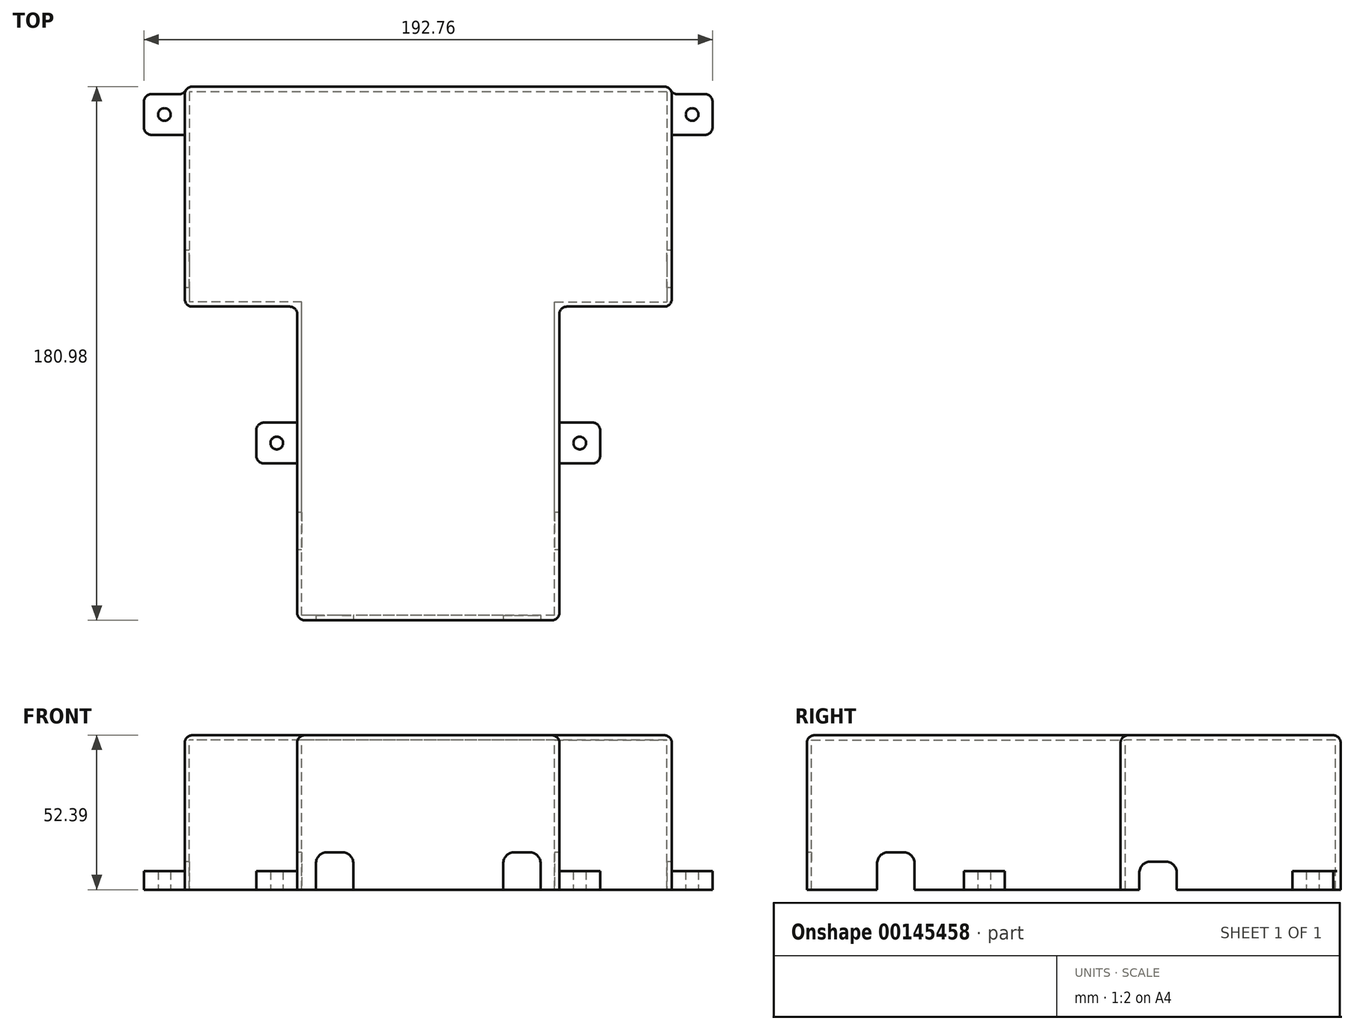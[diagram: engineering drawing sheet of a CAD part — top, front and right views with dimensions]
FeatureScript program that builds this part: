
annotation { "Feature Type Name" : "Feature", "Feature Type Description" : "" }
export const myFeature = defineFeature(function(context is Context, id is Id, definition is map)
    precondition{}
    {
        {
            var Q0;
            Q0=qCreatedBy(makeId("Top.planeOp"),FACE);
            var sketch = newSketch(context, id + "F0", { "sketchPlane" : qUnion([Q0])});
            skLineSegment(sketch, "E0.bottom", {"start": v(-82.55, 90.49) * mm, "end": v(82.55, 90.49) * mm});
            skLineSegment(sketch, "E0.top", {"start": v(-82.55, -90.49) * mm, "end": v(82.55, -90.49) * mm});
            skLineSegment(sketch, "E0.left", {"start": v(-82.55, 90.49) * mm, "end": v(-82.55, -90.49) * mm});
            skLineSegment(sketch, "E0.right", {"start": v(82.55, 90.49) * mm, "end": v(82.55, -90.49) * mm});
            skPoint(sketch, "E0.middle", {"position": v(0, 0) * mm});
            skLineSegment(sketch, "E1.bottom", {"start": v(-76.2, 85.72) * mm, "end": v(76.2, 85.72) * mm, "construction": true});
            skLineSegment(sketch, "E1.top", {"start": v(-76.2, 34.92) * mm, "end": v(76.2, 34.92) * mm, "construction": true});
            skLineSegment(sketch, "E1.left", {"start": v(-76.2, 85.72) * mm, "end": v(-76.2, 34.92) * mm, "construction": true});
            skLineSegment(sketch, "E1.right", {"start": v(76.2, 85.73) * mm, "end": v(76.2, 34.93) * mm, "construction": true});
            skPoint(sketch, "E1.middle", {"position": v(0, 60.32) * mm});
            skLineSegment(sketch, "E2.bottom", {"start": v(-47.62, -3.18) * mm, "end": v(-9.52, -3.18) * mm, "construction": true});
            skLineSegment(sketch, "E2.top", {"start": v(-47.62, -85.73) * mm, "end": v(-9.52, -85.73) * mm, "construction": true});
            skLineSegment(sketch, "E2.left", {"start": v(-47.62, -3.18) * mm, "end": v(-47.62, -85.73) * mm, "construction": true});
            skLineSegment(sketch, "E2.right", {"start": v(-9.52, -3.18) * mm, "end": v(-9.52, -85.73) * mm, "construction": true});
            skPoint(sketch, "E2.middle", {"position": v(-28.57, -44.45) * mm});
            skPoint(sketch, "E3.MirrorP", {"position": v(28.57, -44.45) * mm});
            skLineSegment(sketch, "E4.MirrorCS", {"start": v(47.62, -3.18) * mm, "end": v(47.62, -85.73) * mm, "construction": true});
            skLineSegment(sketch, "E5.MirrorCS", {"start": v(47.62, -85.73) * mm, "end": v(9.52, -85.73) * mm, "construction": true});
            skLineSegment(sketch, "E6.MirrorCS", {"start": v(47.62, -3.18) * mm, "end": v(9.52, -3.18) * mm, "construction": true});
            skLineSegment(sketch, "E7", {"start": v(0, 85.72) * mm, "end": v(0, 90.49) * mm, "construction": true});
            skLineSegment(sketch, "E8", {"start": v(-28.57, -85.73) * mm, "end": v(-28.57, -90.49) * mm, "construction": true});
            skLineSegment(sketch, "E9", {"start": v(-82.55, 15.87) * mm, "end": v(-44.45, 15.87) * mm});
            skLineSegment(sketch, "E10", {"start": v(-44.45, 15.87) * mm, "end": v(-44.45, -90.49) * mm});
            skLineSegment(sketch, "E11.MirrorCS", {"start": v(44.45, 15.87) * mm, "end": v(44.45, -90.49) * mm});
            skLineSegment(sketch, "E12.MirrorCS", {"start": v(82.55, 15.87) * mm, "end": v(44.45, 15.87) * mm});
            skLineSegment(sketch, "E13.bottom", {"start": v(-8.25, -90.49) * mm, "end": v(-6.67, -90.49) * mm});
            skLineSegment(sketch, "E13.top", {"start": v(-8.25, 0) * mm, "end": v(-6.67, 0) * mm});
            skLineSegment(sketch, "E13.right", {"start": v(-6.67, -90.49) * mm, "end": v(-6.67, 0) * mm});
            skLineSegment(sketch, "E14.MirrorCS", {"start": v(8.25, -90.49) * mm, "end": v(8.25, 0) * mm});
            skLineSegment(sketch, "E15.MirrorCS", {"start": v(8.25, 0) * mm, "end": v(6.67, 0) * mm});
            skLineSegment(sketch, "E16.MirrorCS", {"start": v(8.25, -90.49) * mm, "end": v(6.67, -90.49) * mm});
            skLineSegment(sketch, "E17.MirrorCS", {"start": v(9.52, -3.18) * mm, "end": v(9.52, -85.73) * mm, "construction": true});
            skLineSegment(sketch, "E18.bottom", {"start": v(-66.67, 34.13) * mm, "end": v(-41.27, 34.13) * mm});
            skLineSegment(sketch, "E18.top", {"start": v(-66.67, 30.96) * mm, "end": v(-41.27, 30.96) * mm});
            skLineSegment(sketch, "E18.left", {"start": v(-66.68, 34.13) * mm, "end": v(-66.68, 30.96) * mm});
            skLineSegment(sketch, "E18.right", {"start": v(-41.28, 34.13) * mm, "end": v(-41.28, 30.96) * mm});
            skPoint(sketch, "E18.middle", {"position": v(-53.97, 32.54) * mm});
            skLineSegment(sketch, "E19", {"start": v(0, 60.32) * mm, "end": v(-14.3, 60.32) * mm, "construction": true});
            skPoint(sketch, "E20.MirrorP", {"position": v(-53.98, 88.1) * mm});
            skLineSegment(sketch, "E21.MirrorCS", {"start": v(-66.68, 89.7) * mm, "end": v(-41.27, 89.7) * mm});
            skLineSegment(sketch, "E22.MirrorCS", {"start": v(-41.28, 86.52) * mm, "end": v(-41.28, 89.7) * mm});
            skLineSegment(sketch, "E23.MirrorCS", {"start": v(-66.68, 86.52) * mm, "end": v(-66.68, 89.7) * mm});
            skLineSegment(sketch, "E24.MirrorCS", {"start": v(-66.67, 86.52) * mm, "end": v(-41.27, 86.52) * mm});
            skPoint(sketch, "E25.MirrorP", {"position": v(53.98, 32.54) * mm});
            skLineSegment(sketch, "E26.MirrorCS", {"start": v(66.67, 86.52) * mm, "end": v(41.27, 86.52) * mm});
            skLineSegment(sketch, "E27.MirrorCS", {"start": v(66.68, 89.7) * mm, "end": v(41.27, 89.7) * mm});
            skPoint(sketch, "E28.MirrorP", {"position": v(53.98, 88.1) * mm});
            skLineSegment(sketch, "E29.MirrorCS", {"start": v(41.28, 86.52) * mm, "end": v(41.28, 89.7) * mm});
            skLineSegment(sketch, "E30.MirrorCS", {"start": v(66.68, 86.52) * mm, "end": v(66.68, 89.7) * mm});
            skLineSegment(sketch, "E31.MirrorCS", {"start": v(41.28, 34.13) * mm, "end": v(41.28, 30.96) * mm});
            skLineSegment(sketch, "E32.MirrorCS", {"start": v(66.68, 34.13) * mm, "end": v(66.68, 30.96) * mm});
            skLineSegment(sketch, "E33.MirrorCS", {"start": v(66.68, 34.13) * mm, "end": v(41.28, 34.13) * mm});
            skLineSegment(sketch, "E34.MirrorCS", {"start": v(66.68, 30.96) * mm, "end": v(41.28, 30.96) * mm});
            skSolve(sketch);
        }
        {
            var Q0;
            Q0=makeQuery(id+"F0.imprint","IMPRINT",FACE,{"disambiguationData":[TD([[makeQuery(id+"F0.imprint","IMPRINT",EDGE,{"derivedFrom":sQuery(id+"F0.wireOp",EDGE,"E13.bottom")}),1.0]])]});
            var Q1;
            Q1=makeQuery(id+"F0.imprint","IMPRINT",FACE,{"disambiguationData":[TD([[makeQuery(id+"F0.imprint","IMPRINT",EDGE,{"derivedFrom":sQuery(id+"F0.wireOp",EDGE,"E14.MirrorCS")}),1.0]])]});
            var Q2;
            Q2=makeQuery(id+"F0.imprint","IMPRINT",FACE,{"disambiguationData":[TD([[makeQuery(id+"F0.imprint","IMPRINT",EDGE,{"derivedFrom":sQuery(id+"F0.wireOp",EDGE,"E21.MirrorCS")}),-1.0]])]});
            var Q3;
            Q3=makeQuery(id+"F0.imprint","IMPRINT",FACE,{"disambiguationData":[TD([[makeQuery(id+"F0.imprint","IMPRINT",EDGE,{"derivedFrom":sQuery(id+"F0.wireOp",EDGE,"E18.bottom")}),-1.0]])]});
            var Q4;
            Q4=makeQuery(id+"F0.imprint","IMPRINT",FACE,{"disambiguationData":[TD([[makeQuery(id+"F0.imprint","IMPRINT",EDGE,{"derivedFrom":sQuery(id+"F0.wireOp",EDGE,"E26.MirrorCS")}),-1.0]])]});
            var Q5;
            {var subQ10=sQuery(id+"F0.wireOp",EDGE,"E0.bottom");Q5=makeQuery(id+"F0.imprint","IMPRINT",FACE,{"disambiguationData":[TD([[makeQuery(id+"F0.imprint","IMPRINT",EDGE,{"derivedFrom":subQ10}),-1.0]])]});}
            var Q6;
            Q6=makeQuery(id+"F0.imprint","IMPRINT",FACE,{"disambiguationData":[TD([[makeQuery(id+"F0.imprint","IMPRINT",EDGE,{"derivedFrom":sQuery(id+"F0.wireOp",EDGE,"E31.MirrorCS")}),1.0]])]});
            extrude(context, id + "F1", {"entities" : qUnion([Q0, Q1, Q2, Q3, Q4, Q5, Q6]), "depth" : 1.59 * mm});
        }
        {
            var Q0;
            Q0=makeQuery(id+"F1.opExtrude","CAP_FACE",FACE,{"disambiguationData":[OSD([sQuery(id+"F0.wireOp",EDGE,"E0.bottom"),sQuery(id+"F0.wireOp",EDGE,"E0.top"),sQuery(id+"F0.wireOp",EDGE,"E0.left"),sQuery(id+"F0.wireOp",EDGE,"E0.right"),sQuery(id+"F0.wireOp",EDGE,"E9"),sQuery(id+"F0.wireOp",EDGE,"E10"),sQuery(id+"F0.wireOp",EDGE,"E11.MirrorCS"),sQuery(id+"F0.wireOp",EDGE,"E12.MirrorCS")])],"isStart":true});
            var sketch = newSketch(context, id + "F2", { "sketchPlane" : qUnion([Q0])});
            skLineSegment(sketch, "E35", {"start": v(0, 88.9) * mm, "end": v(-42.86, 88.9) * mm});
            skLineSegment(sketch, "E36", {"start": v(-42.86, 88.9) * mm, "end": v(-42.86, -17.46) * mm});
            skLineSegment(sketch, "E37", {"start": v(-42.86, -17.46) * mm, "end": v(-80.96, -17.46) * mm});
            skLineSegment(sketch, "E38", {"start": v(-80.96, -88.7) * mm, "end": v(0, -88.7) * mm});
            skLineSegment(sketch, "E39", {"start": v(-40.48, -88.7) * mm, "end": v(-40.48, -90.3) * mm, "construction": true});
            skLineSegment(sketch, "E40", {"start": v(-80.96, -53.08) * mm, "end": v(-82.55, -53.08) * mm, "construction": true});
            skLineSegment(sketch, "E41", {"start": v(-61.91, -17.46) * mm, "end": v(-61.91, -15.87) * mm, "construction": true});
            skLineSegment(sketch, "E42", {"start": v(-42.86, 35.72) * mm, "end": v(-44.45, 35.72) * mm});
            skLineSegment(sketch, "E43", {"start": v(-21.43, 88.9) * mm, "end": v(-21.43, 90.49) * mm, "construction": true});
            skLineSegment(sketch, "E44.MirrorCS", {"start": v(40.48, -88.7) * mm, "end": v(40.48, -90.3) * mm, "construction": true});
            skLineSegment(sketch, "E45.MirrorCS", {"start": v(80.96, -53.08) * mm, "end": v(82.55, -53.08) * mm, "construction": true});
            skLineSegment(sketch, "E46.MirrorCS", {"start": v(61.91, -17.46) * mm, "end": v(61.91, -15.87) * mm, "construction": true});
            skLineSegment(sketch, "E47.MirrorCS", {"start": v(42.86, 35.72) * mm, "end": v(44.45, 35.72) * mm});
            skLineSegment(sketch, "E48.MirrorCS", {"start": v(21.43, 88.9) * mm, "end": v(21.43, 90.49) * mm, "construction": true});
            skLineSegment(sketch, "E49.MirrorCS", {"start": v(80.96, -88.7) * mm, "end": v(0, -88.7) * mm});
            skLineSegment(sketch, "E50.MirrorCS", {"start": v(42.86, -17.46) * mm, "end": v(80.96, -17.46) * mm});
            skLineSegment(sketch, "E51.MirrorCS", {"start": v(0, 88.9) * mm, "end": v(42.86, 88.9) * mm});
            skLineSegment(sketch, "E52.MirrorCS", {"start": v(42.86, 88.9) * mm, "end": v(42.86, -17.46) * mm});
            skLineSegment(sketch, "E53", {"start": v(-80.96, -88.7) * mm, "end": v(-80.96, -17.46) * mm});
            skLineSegment(sketch, "E54.MirrorCS", {"start": v(80.96, -88.7) * mm, "end": v(80.96, -17.46) * mm});
            skSolve(sketch);
        }
        {
            var Q0;
            {var subQ3=sQuery(id+"F2.wireOp",EDGE,"E35");Q0=makeQuery(id+"F2.imprint","IMPRINT",FACE,{"disambiguationData":[TD([[makeQuery(id+"F2.imprint","IMPRINT",EDGE,{"derivedFrom":subQ3}),-1.0]])]});}
            var Q1;
            {var subQ4=sQuery(id+"F2.wireOp",EDGE,"E37");Q1=makeQuery(id+"F2.imprint","IMPRINT",FACE,{"disambiguationData":[TD([[makeQuery(id+"F2.imprint","IMPRINT",EDGE,{"derivedFrom":subQ4}),-1.0]])]});}
            var Q2;
            {var subQ9=sQuery(id+"F2.wireOp",EDGE,"E42");Q2=makeQuery(id+"F2.imprint","IMPRINT",FACE,{"disambiguationData":[TD([[makeQuery(id+"F2.imprint","IMPRINT",EDGE,{"derivedFrom":subQ9}),-1.0]])]});}
            var Q3;
            {var subQ11=sQuery(id+"F2.wireOp",EDGE,"E47.MirrorCS");Q3=makeQuery(id+"F2.imprint","IMPRINT",FACE,{"disambiguationData":[TD([[makeQuery(id+"F2.imprint","IMPRINT",EDGE,{"derivedFrom":subQ11}),1.0]])]});}
            extrude(context, id + "F3", {"entities" : qUnion([Q0, Q1, Q2, Q3]), "operationType" : NewBodyOperationType.ADD, "offsetDistance" : 25.4 * mm, "depth" : 50.8 * mm});
        }
        {
            var Q0;
            {var subQ0=sQuery(id+"F0.wireOp",EDGE,"E0.top");Q0=makeQuery(id+"F3.boolean.opBoolean","MERGE",FACE,{"derivedFrom":[makeQuery(id+"F1.opExtrude","SWEPT_FACE",FACE,{"disambiguationData":[OSD([subQ0])]}),makeQuery(id+"F3.opExtrude","SWEPT_FACE",FACE,{"disambiguationData":[OSD([subQ0])]})]});}
            var sketch = newSketch(context, id + "F4", { "sketchPlane" : qUnion([Q0])});
            skLineSegment(sketch, "E55", {"start": v(0, -24.6) * mm, "end": v(-25.4, -24.6) * mm, "construction": true});
            skPoint(sketch, "E55.startSnap0", {"position": v(-44.45, -24.6) * mm});
            skLineSegment(sketch, "E56.bottom", {"start": v(-25.4, -50.8) * mm, "end": v(-38.1, -50.8) * mm});
            skLineSegment(sketch, "E56.top", {"start": v(-29.21, -38.1) * mm, "end": v(-34.29, -38.1) * mm});
            skLineSegment(sketch, "E56.left", {"start": v(-25.4, -50.8) * mm, "end": v(-25.4, -41.91) * mm});
            skLineSegment(sketch, "E56.right", {"start": v(-38.1, -50.8) * mm, "end": v(-38.1, -41.91) * mm});
            skLineSegment(sketch, "E57.MirrorCS", {"start": v(25.4, -50.8) * mm, "end": v(25.4, -41.9) * mm});
            skLineSegment(sketch, "E58.MirrorCS", {"start": v(25.4, -50.8) * mm, "end": v(38.1, -50.8) * mm});
            skLineSegment(sketch, "E59.MirrorCS", {"start": v(29.21, -38.1) * mm, "end": v(34.29, -38.1) * mm});
            skLineSegment(sketch, "E60.MirrorCS", {"start": v(38.1, -50.8) * mm, "end": v(38.1, -41.91) * mm});
            skPoint(sketch, "E61.visualSharp", {"position": v(-38.1, -38.1) * mm});
            skArc(sketch, "E61.filletArc", {"start": v(-34.29, -38.1) * mm, "mid": v(-36.98, -39.22) * mm, "end": v(-38.1, -41.91) * mm});
            skPoint(sketch, "E62.visualSharp", {"position": v(-25.4, -38.1) * mm});
            skArc(sketch, "E62.filletArc", {"start": v(-25.4, -41.91) * mm, "mid": v(-26.52, -39.22) * mm, "end": v(-29.21, -38.1) * mm});
            skPoint(sketch, "E63.visualSharp", {"position": v(25.4, -38.1) * mm});
            skArc(sketch, "E63.filletArc", {"start": v(29.21, -38.1) * mm, "mid": v(26.52, -39.22) * mm, "end": v(25.4, -41.9) * mm});
            skPoint(sketch, "E64.visualSharp", {"position": v(38.1, -38.1) * mm});
            skArc(sketch, "E64.filletArc", {"start": v(38.1, -41.91) * mm, "mid": v(36.98, -39.22) * mm, "end": v(34.29, -38.1) * mm});
            skSolve(sketch);
        }
        {
            var Q0;
            Q0 = qSketchRegion(id + "F4", true);
            var Q1;
            Q1=makeQuery(id+"F3.opExtrude","SWEPT_FACE",FACE,{"disambiguationData":[OSD([sQuery(id+"F2.wireOp",EDGE,"E35"),sQuery(id+"F2.wireOp",EDGE,"E51.MirrorCS")])]});
            extrude(context, id + "F5", {"entities" : qUnion([Q0]), "operationType" : NewBodyOperationType.REMOVE, "endBound" : BoundingType.UP_TO_SURFACE, "oppositeDirection" : true, "endBoundEntityFace" : qUnion([Q1]), "depth" : 25.4 * mm});
        }
        {
            var Q0;
            {var subQ0=sQuery(id+"F0.wireOp",EDGE,"E0.left");Q0=makeQuery(id+"F3.boolean.opBoolean","MERGE",FACE,{"derivedFrom":[makeQuery(id+"F1.opExtrude","SWEPT_FACE",FACE,{"disambiguationData":[OSD([subQ0])]}),makeQuery(id+"F3.opExtrude","SWEPT_FACE",FACE,{"disambiguationData":[OSD([subQ0])]})]});}
            var sketch = newSketch(context, id + "F6", { "sketchPlane" : qUnion([Q0])});
            skPoint(sketch, "E65.0", {"position": v(-34.92, 0) * mm});
            skLineSegment(sketch, "E66.bottom", {"start": v(-31.11, -41.28) * mm, "end": v(-26.03, -41.28) * mm});
            skLineSegment(sketch, "E66.top", {"start": v(-34.92, -50.8) * mm, "end": v(-22.22, -50.8) * mm});
            skLineSegment(sketch, "E66.left", {"start": v(-34.92, -45.09) * mm, "end": v(-34.92, -50.8) * mm});
            skLineSegment(sketch, "E66.right", {"start": v(-22.22, -45.09) * mm, "end": v(-22.22, -50.8) * mm});
            skPoint(sketch, "E67.visualSharp", {"position": v(-34.92, -41.28) * mm});
            skArc(sketch, "E67.filletArc", {"start": v(-31.11, -41.28) * mm, "mid": v(-33.8, -42.4) * mm, "end": v(-34.92, -45.09) * mm});
            skPoint(sketch, "E68.visualSharp", {"position": v(-22.22, -41.28) * mm});
            skArc(sketch, "E68.filletArc", {"start": v(-22.22, -45.09) * mm, "mid": v(-23.34, -42.4) * mm, "end": v(-26.03, -41.28) * mm});
            skSolve(sketch);
        }
        {
            var Q0;
            Q0=makeQuery(id+"F6.imprint","IMPRINT",FACE,{"disambiguationData":[TD([[makeQuery(id+"F6.imprint","IMPRINT",EDGE,{"derivedFrom":sQuery(id+"F6.wireOp",EDGE,"E66.bottom")}),-1.0]])]});
            var Q1;
            {var subQ0=sQuery(id+"F0.wireOp",EDGE,"E0.right");Q1=makeQuery(id+"F3.boolean.opBoolean","MERGE",FACE,{"derivedFrom":[makeQuery(id+"F1.opExtrude","SWEPT_FACE",FACE,{"disambiguationData":[OSD([subQ0])]}),makeQuery(id+"F3.opExtrude","SWEPT_FACE",FACE,{"disambiguationData":[OSD([subQ0])]})]});}
            extrude(context, id + "F7", {"entities" : qUnion([Q0]), "operationType" : NewBodyOperationType.REMOVE, "endBound" : BoundingType.UP_TO_SURFACE, "oppositeDirection" : true, "endBoundEntityFace" : qUnion([Q1]), "depth" : 25.4 * mm});
        }
        {
            var Q0;
            {var subQ0=sQuery(id+"F0.wireOp",EDGE,"E10");Q0=makeQuery(id+"F3.boolean.opBoolean","MERGE",FACE,{"derivedFrom":[makeQuery(id+"F1.opExtrude","SWEPT_FACE",FACE,{"disambiguationData":[OSD([subQ0])]}),makeQuery(id+"F3.opExtrude","SWEPT_FACE",FACE,{"disambiguationData":[OSD([subQ0])]})]});}
            var sketch = newSketch(context, id + "F8", { "sketchPlane" : qUnion([Q0])});
            skPoint(sketch, "E69.0", {"position": v(85.73, 0) * mm});
            skLineSegment(sketch, "E70", {"start": v(85.73, 0) * mm, "end": v(66.68, 0) * mm, "construction": true});
            skLineSegment(sketch, "E71.bottom", {"start": v(66.68, -50.8) * mm, "end": v(53.98, -50.8) * mm});
            skLineSegment(sketch, "E71.top", {"start": v(62.87, -38.1) * mm, "end": v(57.79, -38.1) * mm});
            skLineSegment(sketch, "E71.left", {"start": v(66.68, -50.8) * mm, "end": v(66.68, -41.91) * mm});
            skLineSegment(sketch, "E71.right", {"start": v(53.98, -50.8) * mm, "end": v(53.98, -41.91) * mm});
            skPoint(sketch, "E72.visualSharp", {"position": v(53.98, -38.1) * mm});
            skArc(sketch, "E72.filletArc", {"start": v(57.79, -38.1) * mm, "mid": v(55.1, -39.22) * mm, "end": v(53.98, -41.91) * mm});
            skPoint(sketch, "E73.visualSharp", {"position": v(66.68, -38.1) * mm});
            skArc(sketch, "E73.filletArc", {"start": v(66.68, -41.91) * mm, "mid": v(65.56, -39.22) * mm, "end": v(62.87, -38.1) * mm});
            skSolve(sketch);
        }
        {
            var Q0;
            Q0 = qSketchRegion(id + "F8", true);
            var Q1;
            {var subQ0=sQuery(id+"F0.wireOp",EDGE,"E11.MirrorCS");Q1=makeQuery(id+"F3.boolean.opBoolean","MERGE",FACE,{"derivedFrom":[makeQuery(id+"F1.opExtrude","SWEPT_FACE",FACE,{"disambiguationData":[OSD([subQ0])]}),makeQuery(id+"F3.opExtrude","SWEPT_FACE",FACE,{"disambiguationData":[OSD([subQ0])]})]});}
            extrude(context, id + "F9", {"entities" : qUnion([Q0]), "operationType" : NewBodyOperationType.REMOVE, "endBound" : BoundingType.UP_TO_SURFACE, "oppositeDirection" : true, "endBoundEntityFace" : qUnion([Q1]), "depth" : 25.4 * mm});
        }
        {
            var Q0;
            Q0=makeQuery(id+"F1.opExtrude","CAP_EDGE",EDGE,{"disambiguationData":[OSD([sQuery(id+"F0.wireOp",EDGE,"E0.left")])],"isStart":false});
            var Q1;
            Q1=makeQuery(id+"F1.opExtrude","CAP_EDGE",EDGE,{"disambiguationData":[OSD([sQuery(id+"F0.wireOp",EDGE,"E10")])],"isStart":false});
            var Q2;
            Q2=makeQuery(id+"F1.opExtrude","CAP_EDGE",EDGE,{"disambiguationData":[OSD([sQuery(id+"F0.wireOp",EDGE,"E9")])],"isStart":false});
            var Q3;
            Q3=makeQuery(id+"F1.opExtrude","CAP_EDGE",EDGE,{"disambiguationData":[OSD([sQuery(id+"F0.wireOp",EDGE,"E0.top"),sQuery(id+"F0.wireOp",EDGE,"E13.bottom"),sQuery(id+"F0.wireOp",EDGE,"E16.MirrorCS")])],"isStart":false});
            var Q4;
            Q4=makeQuery(id+"F1.opExtrude","CAP_EDGE",EDGE,{"disambiguationData":[OSD([sQuery(id+"F0.wireOp",EDGE,"E11.MirrorCS")])],"isStart":false});
            var Q5;
            Q5=makeQuery(id+"F1.opExtrude","CAP_EDGE",EDGE,{"disambiguationData":[OSD([sQuery(id+"F0.wireOp",EDGE,"E12.MirrorCS")])],"isStart":false});
            var Q6;
            Q6=makeQuery(id+"F1.opExtrude","CAP_EDGE",EDGE,{"disambiguationData":[OSD([sQuery(id+"F0.wireOp",EDGE,"E0.right")])],"isStart":false});
            var Q7;
            Q7=makeQuery(id+"F1.opExtrude","CAP_EDGE",EDGE,{"disambiguationData":[OSD([sQuery(id+"F0.wireOp",EDGE,"E0.bottom")])],"isStart":false});
            var Q8;
            {var subQ0=sQuery(id+"F0.wireOp",EDGE,"E0.right");var subQ1=sQuery(id+"F0.wireOp",EDGE,"E0.bottom");Q8=makeQuery(id+"F3.boolean.opBoolean","MERGE",EDGE,{"derivedFrom":[makeQuery(id+"F1.opExtrude","SWEPT_EDGE",EDGE,{"disambiguationData":[OSD([subQ1,subQ0])]}),makeQuery(id+"F3.opExtrude","SWEPT_EDGE",EDGE,{"disambiguationData":[OSD([subQ1,subQ0])]})]});}
            var Q9;
            {var subQ0=sQuery(id+"F0.wireOp",EDGE,"E0.left");var subQ1=sQuery(id+"F0.wireOp",EDGE,"E0.bottom");Q9=makeQuery(id+"F3.boolean.opBoolean","MERGE",EDGE,{"derivedFrom":[makeQuery(id+"F1.opExtrude","SWEPT_EDGE",EDGE,{"disambiguationData":[OSD([subQ1,subQ0])]}),makeQuery(id+"F3.opExtrude","SWEPT_EDGE",EDGE,{"disambiguationData":[OSD([subQ1,subQ0])]})]});}
            var Q10;
            {var subQ0=sQuery(id+"F0.wireOp",EDGE,"E9");var subQ1=sQuery(id+"F0.wireOp",EDGE,"E0.left");Q10=makeQuery(id+"F3.boolean.opBoolean","MERGE",EDGE,{"derivedFrom":[makeQuery(id+"F1.opExtrude","SWEPT_EDGE",EDGE,{"disambiguationData":[OSD([subQ1,subQ0])]}),makeQuery(id+"F3.opExtrude","SWEPT_EDGE",EDGE,{"disambiguationData":[OSD([subQ1,subQ0])]})]});}
            var Q11;
            {var subQ0=sQuery(id+"F0.wireOp",EDGE,"E10");var subQ1=sQuery(id+"F0.wireOp",EDGE,"E9");Q11=makeQuery(id+"F3.boolean.opBoolean","MERGE",EDGE,{"derivedFrom":[makeQuery(id+"F1.opExtrude","SWEPT_EDGE",EDGE,{"disambiguationData":[OSD([subQ1,subQ0])]}),makeQuery(id+"F3.opExtrude","SWEPT_EDGE",EDGE,{"disambiguationData":[OSD([subQ1,subQ0])]})]});}
            var Q12;
            {var subQ0=sQuery(id+"F0.wireOp",EDGE,"E10");var subQ1=sQuery(id+"F0.wireOp",EDGE,"E0.top");Q12=makeQuery(id+"F3.boolean.opBoolean","MERGE",EDGE,{"derivedFrom":[makeQuery(id+"F1.opExtrude","SWEPT_EDGE",EDGE,{"disambiguationData":[OSD([subQ1,subQ0])]}),makeQuery(id+"F3.opExtrude","SWEPT_EDGE",EDGE,{"disambiguationData":[OSD([subQ1,subQ0,sQuery(id+"F0.wireOp",EDGE,"E13.bottom"),sQuery(id+"F0.wireOp",EDGE,"E16.MirrorCS")])]})]});}
            var Q13;
            {var subQ0=sQuery(id+"F0.wireOp",EDGE,"E11.MirrorCS");var subQ1=sQuery(id+"F0.wireOp",EDGE,"E0.top");Q13=makeQuery(id+"F3.boolean.opBoolean","MERGE",EDGE,{"derivedFrom":[makeQuery(id+"F1.opExtrude","SWEPT_EDGE",EDGE,{"disambiguationData":[OSD([subQ1,subQ0])]}),makeQuery(id+"F3.opExtrude","SWEPT_EDGE",EDGE,{"disambiguationData":[OSD([subQ1,subQ0,sQuery(id+"F0.wireOp",EDGE,"E13.bottom"),sQuery(id+"F0.wireOp",EDGE,"E16.MirrorCS")])]})]});}
            var Q14;
            {var subQ0=sQuery(id+"F0.wireOp",EDGE,"E12.MirrorCS");var subQ1=sQuery(id+"F0.wireOp",EDGE,"E11.MirrorCS");Q14=makeQuery(id+"F3.boolean.opBoolean","MERGE",EDGE,{"derivedFrom":[makeQuery(id+"F1.opExtrude","SWEPT_EDGE",EDGE,{"disambiguationData":[OSD([subQ1,subQ0])]}),makeQuery(id+"F3.opExtrude","SWEPT_EDGE",EDGE,{"disambiguationData":[OSD([subQ1,subQ0])]})]});}
            var Q15;
            {var subQ0=sQuery(id+"F0.wireOp",EDGE,"E12.MirrorCS");var subQ1=sQuery(id+"F0.wireOp",EDGE,"E0.right");Q15=makeQuery(id+"F3.boolean.opBoolean","MERGE",EDGE,{"derivedFrom":[makeQuery(id+"F1.opExtrude","SWEPT_EDGE",EDGE,{"disambiguationData":[OSD([subQ1,subQ0])]}),makeQuery(id+"F3.opExtrude","SWEPT_EDGE",EDGE,{"disambiguationData":[OSD([subQ1,subQ0])]})]});}
            fillet(context, id + "F10", {"entities" : qUnion([Q0, Q1, Q2, Q3, Q4, Q5, Q6, Q7, Q8, Q9, Q10, Q11, Q12, Q13, Q14, Q15]), "radius" : 2.54 * mm, "tangentPropagation" : true, "allowEdgeOverflow" : false});
        }
        {
            var Q0;
            {var subQ1=sQuery(id+"F0.wireOp",EDGE,"E10");var subQ3=sQuery(id+"F0.wireOp",EDGE,"E0.left");var subQ5=sQuery(id+"F2.wireOp",EDGE,"E37");var subQ7=sQuery(id+"F0.wireOp",EDGE,"E9");var subQ8=makeQuery(id+"F1.opExtrude","SWEPT_FACE",FACE,{"disambiguationData":[OSD([subQ7])]});var subQ9=sQuery(id+"F2.wireOp",EDGE,"4HbXZCzy-srsC-K1ag-yFP5-efG93YVFuTpm");var subQ13=makeQuery(id+"F1.opExtrude","SWEPT_FACE",FACE,{"disambiguationData":[OSD([subQ3])]});var subQ14=sQuery(id+"F2.wireOp",EDGE,"E36");var subQ16=sQuery(id+"F2.wireOp",EDGE,"E35");var subQ18=sQuery(id+"F0.wireOp",EDGE,"E16.MirrorCS");var subQ20=sQuery(id+"F0.wireOp",EDGE,"E11.MirrorCS");var subQ22=sQuery(id+"F0.wireOp",EDGE,"E13.bottom");var subQ23=sQuery(id+"F0.wireOp",EDGE,"E0.top");var subQ26=sQuery(id+"F0.wireOp",EDGE,"E12.MirrorCS");var subQ27=sQuery(id+"F0.wireOp",EDGE,"E0.right");var subQ28=sQuery(id+"F0.wireOp",EDGE,"E0.bottom");var subQ30=sQuery(id+"F0.wireOp",EDGE,"E14.MirrorCS");var subQ33=sQuery(id+"F0.wireOp",EDGE,"E13.left");var subQ37=sQuery(id+"F2.wireOp",EDGE,"E52.MirrorCS");var subQ38=sQuery(id+"F2.wireOp",EDGE,"E51.MirrorCS");var subQ39=sQuery(id+"F2.wireOp",EDGE,"E50.MirrorCS");var subQ40=sQuery(id+"F2.wireOp",EDGE,"E49.MirrorCS");var subQ41=sQuery(id+"F2.wireOp",EDGE,"E38");var subQ42=sQuery(id+"F2.wireOp",EDGE,"49bd3e88-0498-4bd4-9d24-909cf07a791b6.MirrorCS");Q0=makeQuery(id+"F9.boolean.opBoolean","SPLIT",FACE,{"disambiguationData":[TD([subQ13])],"derivedFrom":makeQuery(id+"F7.boolean.opBoolean","SPLIT",FACE,{"disambiguationData":[TD([subQ8])],"derivedFrom":makeQuery(id+"F5.boolean.opBoolean","SPLIT",FACE,{"disambiguationData":[TD([makeQuery(id+"F1.opExtrude","SWEPT_FACE",FACE,{"disambiguationData":[OSD([subQ28])]})])],"derivedFrom":makeQuery(id+"F3.opExtrude","CAP_FACE",FACE,{"disambiguationData":[OSD([subQ28,subQ23,subQ3,subQ27,subQ7,subQ1,subQ20,subQ26,subQ22,subQ33,subQ30,subQ18,subQ16,subQ14,subQ5,subQ9,subQ41,subQ40,subQ42,subQ39,subQ38,subQ37])],"isStart":false})})})});}
            var sketch = newSketch(context, id + "F11", { "sketchPlane" : qUnion([Q0])});
            skPoint(sketch, "E74.0", {"position": v(-82.55, -87.95) * mm});
            skLineSegment(sketch, "E75.bottom", {"start": v(-82.55, -87.95) * mm, "end": v(-96.38, -87.95) * mm});
            skLineSegment(sketch, "E75.top", {"start": v(-82.55, -74.12) * mm, "end": v(-96.38, -74.12) * mm});
            skLineSegment(sketch, "E75.left", {"start": v(-82.55, -87.95) * mm, "end": v(-82.55, -74.12) * mm});
            skLineSegment(sketch, "E75.right", {"start": v(-96.38, -87.95) * mm, "end": v(-96.38, -74.12) * mm});
            skLineSegment(sketch, "E76", {"start": v(-96.38, -74.12) * mm, "end": v(-82.55, -87.95) * mm, "construction": true});
            skCircle(sketch, "E77", {"center": v(-89.47, -81.03) * mm, "radius": 2.15 * mm});
            skLineSegment(sketch, "E78.MirrorCS", {"start": v(96.38, -74.12) * mm, "end": v(82.55, -87.95) * mm, "construction": true});
            skCircle(sketch, "E79.MirrorC", {"center": v(89.47, -81.03) * mm, "radius": 2.15 * mm});
            skLineSegment(sketch, "E80.MirrorCS", {"start": v(82.55, -74.12) * mm, "end": v(96.38, -74.12) * mm});
            skLineSegment(sketch, "E81.MirrorCS", {"start": v(82.55, -87.95) * mm, "end": v(82.55, -74.12) * mm});
            skLineSegment(sketch, "E82.MirrorCS", {"start": v(96.38, -87.95) * mm, "end": v(96.38, -74.12) * mm});
            skLineSegment(sketch, "E83.MirrorCS", {"start": v(82.55, -87.95) * mm, "end": v(96.38, -87.95) * mm});
            skPoint(sketch, "E84.MirrorP", {"position": v(82.55, -87.95) * mm});
            skPoint(sketch, "E85.0", {"position": v(-44.45, 37.3) * mm});
            skLineSegment(sketch, "E86.bottom", {"start": v(-44.45, 37.3) * mm, "end": v(-58.28, 37.3) * mm});
            skLineSegment(sketch, "E86.top", {"start": v(-44.45, 23.48) * mm, "end": v(-58.28, 23.48) * mm});
            skLineSegment(sketch, "E86.left", {"start": v(-44.45, 37.3) * mm, "end": v(-44.45, 23.48) * mm});
            skLineSegment(sketch, "E86.right", {"start": v(-58.28, 37.3) * mm, "end": v(-58.28, 23.48) * mm});
            skLineSegment(sketch, "E87", {"start": v(-58.28, 37.3) * mm, "end": v(-44.45, 23.48) * mm, "construction": true});
            skCircle(sketch, "E88", {"center": v(-51.37, 30.4) * mm, "radius": 2.15 * mm});
            skLineSegment(sketch, "E89.MirrorCS", {"start": v(58.28, 37.3) * mm, "end": v(44.45, 23.48) * mm, "construction": true});
            skPoint(sketch, "E90.MirrorP", {"position": v(44.45, 37.3) * mm});
            skLineSegment(sketch, "E91.MirrorCS", {"start": v(44.45, 23.48) * mm, "end": v(58.28, 23.48) * mm});
            skLineSegment(sketch, "E92.MirrorCS", {"start": v(44.45, 37.3) * mm, "end": v(44.45, 23.48) * mm});
            skLineSegment(sketch, "E93.MirrorCS", {"start": v(58.28, 37.3) * mm, "end": v(58.28, 23.48) * mm});
            skLineSegment(sketch, "E94.MirrorCS", {"start": v(44.45, 37.3) * mm, "end": v(58.28, 37.3) * mm});
            skCircle(sketch, "E95.MirrorC", {"center": v(51.37, 30.4) * mm, "radius": 2.15 * mm});
            skSolve(sketch);
        }
        {
            var Q0;
            Q0 = qSketchRegion(id + "F11", true);
            extrude(context, id + "F12", {"entities" : qUnion([Q0]), "operationType" : NewBodyOperationType.ADD, "oppositeDirection" : true, "depth" : 6.35 * mm});
        }
        {
            var Q0;
            Q0=makeQuery(id+"F12.opExtrude","SWEPT_EDGE",EDGE,{"disambiguationData":[OSD([sQuery(id+"F0.wireOp",EDGE,"E10"),sQuery(id+"F11.wireOp",EDGE,"E86.bottom"),sQuery(id+"F11.wireOp",EDGE,"E86.left")])]});
            var Q1;
            Q1=makeQuery(id+"F12.opExtrude","SWEPT_EDGE",EDGE,{"disambiguationData":[OSD([sQuery(id+"F0.wireOp",EDGE,"E10"),sQuery(id+"F11.wireOp",EDGE,"E86.top"),sQuery(id+"F11.wireOp",EDGE,"E86.left")])]});
            var Q2;
            Q2=makeQuery(id+"F12.opExtrude","SWEPT_EDGE",EDGE,{"disambiguationData":[OSD([sQuery(id+"F11.wireOp",EDGE,"E86.top"),sQuery(id+"F11.wireOp",EDGE,"E86.right")])]});
            var Q3;
            Q3=makeQuery(id+"F12.opExtrude","SWEPT_EDGE",EDGE,{"disambiguationData":[OSD([sQuery(id+"F11.wireOp",EDGE,"E86.bottom"),sQuery(id+"F11.wireOp",EDGE,"E86.right")])]});
            var Q4;
            Q4=makeQuery(id+"F12.opExtrude","SWEPT_EDGE",EDGE,{"disambiguationData":[OSD([sQuery(id+"F11.wireOp",EDGE,"E92.MirrorCS"),sQuery(id+"F11.wireOp",EDGE,"E94.MirrorCS")])]});
            var Q5;
            Q5=makeQuery(id+"F12.opExtrude","SWEPT_EDGE",EDGE,{"disambiguationData":[OSD([sQuery(id+"F11.wireOp",EDGE,"E91.MirrorCS"),sQuery(id+"F11.wireOp",EDGE,"E92.MirrorCS")])]});
            var Q6;
            Q6=makeQuery(id+"F12.opExtrude","SWEPT_EDGE",EDGE,{"disambiguationData":[OSD([sQuery(id+"F11.wireOp",EDGE,"E91.MirrorCS"),sQuery(id+"F11.wireOp",EDGE,"E93.MirrorCS")])]});
            var Q7;
            Q7=makeQuery(id+"F12.opExtrude","SWEPT_EDGE",EDGE,{"disambiguationData":[OSD([sQuery(id+"F11.wireOp",EDGE,"E93.MirrorCS"),sQuery(id+"F11.wireOp",EDGE,"E94.MirrorCS")])]});
            var Q8;
            Q8=makeQuery(id+"F12.opExtrude","SWEPT_EDGE",EDGE,{"disambiguationData":[OSD([sQuery(id+"F11.wireOp",EDGE,"E80.MirrorCS"),sQuery(id+"F11.wireOp",EDGE,"E81.MirrorCS")])]});
            var Q9;
            Q9=makeQuery(id+"F12.opExtrude","SWEPT_EDGE",EDGE,{"disambiguationData":[OSD([sQuery(id+"F11.wireOp",EDGE,"E80.MirrorCS"),sQuery(id+"F11.wireOp",EDGE,"E82.MirrorCS")])]});
            var Q10;
            Q10=makeQuery(id+"F12.opExtrude","SWEPT_EDGE",EDGE,{"disambiguationData":[OSD([sQuery(id+"F11.wireOp",EDGE,"E82.MirrorCS"),sQuery(id+"F11.wireOp",EDGE,"E83.MirrorCS")])]});
            var Q11;
            {var subQ0=sQuery(id+"F0.wireOp",EDGE,"E0.right");var subQ1=sQuery(id+"F0.wireOp",EDGE,"E0.bottom");Q11=makeQuery(id+"F12.boolean.opBoolean","MERGE",EDGE,{"derivedFrom":[makeQuery(id+"F10.opFillet","BLEND_EDGE",EDGE,{"blendedFrom":[makeQuery(id+"F3.boolean.opBoolean","MERGE",EDGE,{"derivedFrom":[makeQuery(id+"F1.opExtrude","SWEPT_EDGE",EDGE,{"disambiguationData":[OSD([subQ1,subQ0])]}),makeQuery(id+"F3.opExtrude","SWEPT_EDGE",EDGE,{"disambiguationData":[OSD([subQ1,subQ0])]})]}),makeQuery(id+"F3.boolean.opBoolean","MERGE",FACE,{"derivedFrom":[makeQuery(id+"F1.opExtrude","SWEPT_FACE",FACE,{"disambiguationData":[OSD([subQ0])]}),makeQuery(id+"F3.opExtrude","SWEPT_FACE",FACE,{"disambiguationData":[OSD([subQ0])]})]})],"blendedInto":[makeQuery(id+"F3.boolean.opBoolean","MERGE",FACE,{"derivedFrom":[makeQuery(id+"F1.opExtrude","SWEPT_FACE",FACE,{"disambiguationData":[OSD([subQ0])]}),makeQuery(id+"F3.opExtrude","SWEPT_FACE",FACE,{"disambiguationData":[OSD([subQ0])]})]})]}),makeQuery(id+"F12.opExtrude","SWEPT_EDGE",EDGE,{"disambiguationData":[OSD([sQuery(id+"F11.wireOp",EDGE,"E81.MirrorCS"),sQuery(id+"F11.wireOp",EDGE,"E83.MirrorCS")])]})]});}
            var Q12;
            {var subQ0=sQuery(id+"F0.wireOp",EDGE,"E0.left");var subQ1=sQuery(id+"F0.wireOp",EDGE,"E0.bottom");Q12=makeQuery(id+"F12.boolean.opBoolean","MERGE",EDGE,{"derivedFrom":[makeQuery(id+"F10.opFillet","BLEND_EDGE",EDGE,{"blendedFrom":[makeQuery(id+"F3.boolean.opBoolean","MERGE",EDGE,{"derivedFrom":[makeQuery(id+"F1.opExtrude","SWEPT_EDGE",EDGE,{"disambiguationData":[OSD([subQ1,subQ0])]}),makeQuery(id+"F3.opExtrude","SWEPT_EDGE",EDGE,{"disambiguationData":[OSD([subQ1,subQ0])]})]}),makeQuery(id+"F3.boolean.opBoolean","MERGE",FACE,{"derivedFrom":[makeQuery(id+"F1.opExtrude","SWEPT_FACE",FACE,{"disambiguationData":[OSD([subQ0])]}),makeQuery(id+"F3.opExtrude","SWEPT_FACE",FACE,{"disambiguationData":[OSD([subQ0])]})]})],"blendedInto":[makeQuery(id+"F3.boolean.opBoolean","MERGE",FACE,{"derivedFrom":[makeQuery(id+"F1.opExtrude","SWEPT_FACE",FACE,{"disambiguationData":[OSD([subQ0])]}),makeQuery(id+"F3.opExtrude","SWEPT_FACE",FACE,{"disambiguationData":[OSD([subQ0])]})]})]}),makeQuery(id+"F12.opExtrude","SWEPT_EDGE",EDGE,{"disambiguationData":[OSD([sQuery(id+"F11.wireOp",EDGE,"E75.bottom"),sQuery(id+"F11.wireOp",EDGE,"E75.left")])]})]});}
            var Q13;
            Q13=makeQuery(id+"F12.opExtrude","SWEPT_EDGE",EDGE,{"disambiguationData":[OSD([sQuery(id+"F11.wireOp",EDGE,"E75.bottom"),sQuery(id+"F11.wireOp",EDGE,"E75.right")])]});
            var Q14;
            Q14=makeQuery(id+"F12.opExtrude","SWEPT_EDGE",EDGE,{"disambiguationData":[OSD([sQuery(id+"F11.wireOp",EDGE,"E75.top"),sQuery(id+"F11.wireOp",EDGE,"E75.left")])]});
            var Q15;
            Q15=makeQuery(id+"F12.opExtrude","SWEPT_EDGE",EDGE,{"disambiguationData":[OSD([sQuery(id+"F11.wireOp",EDGE,"E75.top"),sQuery(id+"F11.wireOp",EDGE,"E75.right")])]});
            var Q16;
            Q16=makeQuery(id+"F12.opExtrude","CAP_EDGE",EDGE,{"disambiguationData":[OSD([sQuery(id+"F11.wireOp",EDGE,"E75.left")])],"isStart":false});
            var Q17;
            Q17=makeQuery(id+"F12.opExtrude","CAP_EDGE",EDGE,{"disambiguationData":[OSD([sQuery(id+"F11.wireOp",EDGE,"E86.left")])],"isStart":false});
            var Q18;
            Q18=makeQuery(id+"F12.opExtrude","CAP_EDGE",EDGE,{"disambiguationData":[OSD([sQuery(id+"F11.wireOp",EDGE,"E92.MirrorCS")])],"isStart":false});
            var Q19;
            Q19=makeQuery(id+"F12.opExtrude","CAP_EDGE",EDGE,{"disambiguationData":[OSD([sQuery(id+"F11.wireOp",EDGE,"E81.MirrorCS")])],"isStart":false});
            fillet(context, id + "F13", {"entities" : qUnion([Q0, Q1, Q2, Q3, Q4, Q5, Q6, Q7, Q8, Q9, Q10, Q11, Q12, Q13, Q14, Q15, Q16, Q17, Q18, Q19]), "radius" : 2.54 * mm, "tangentPropagation" : true, "allowEdgeOverflow" : false});
        }
    });
